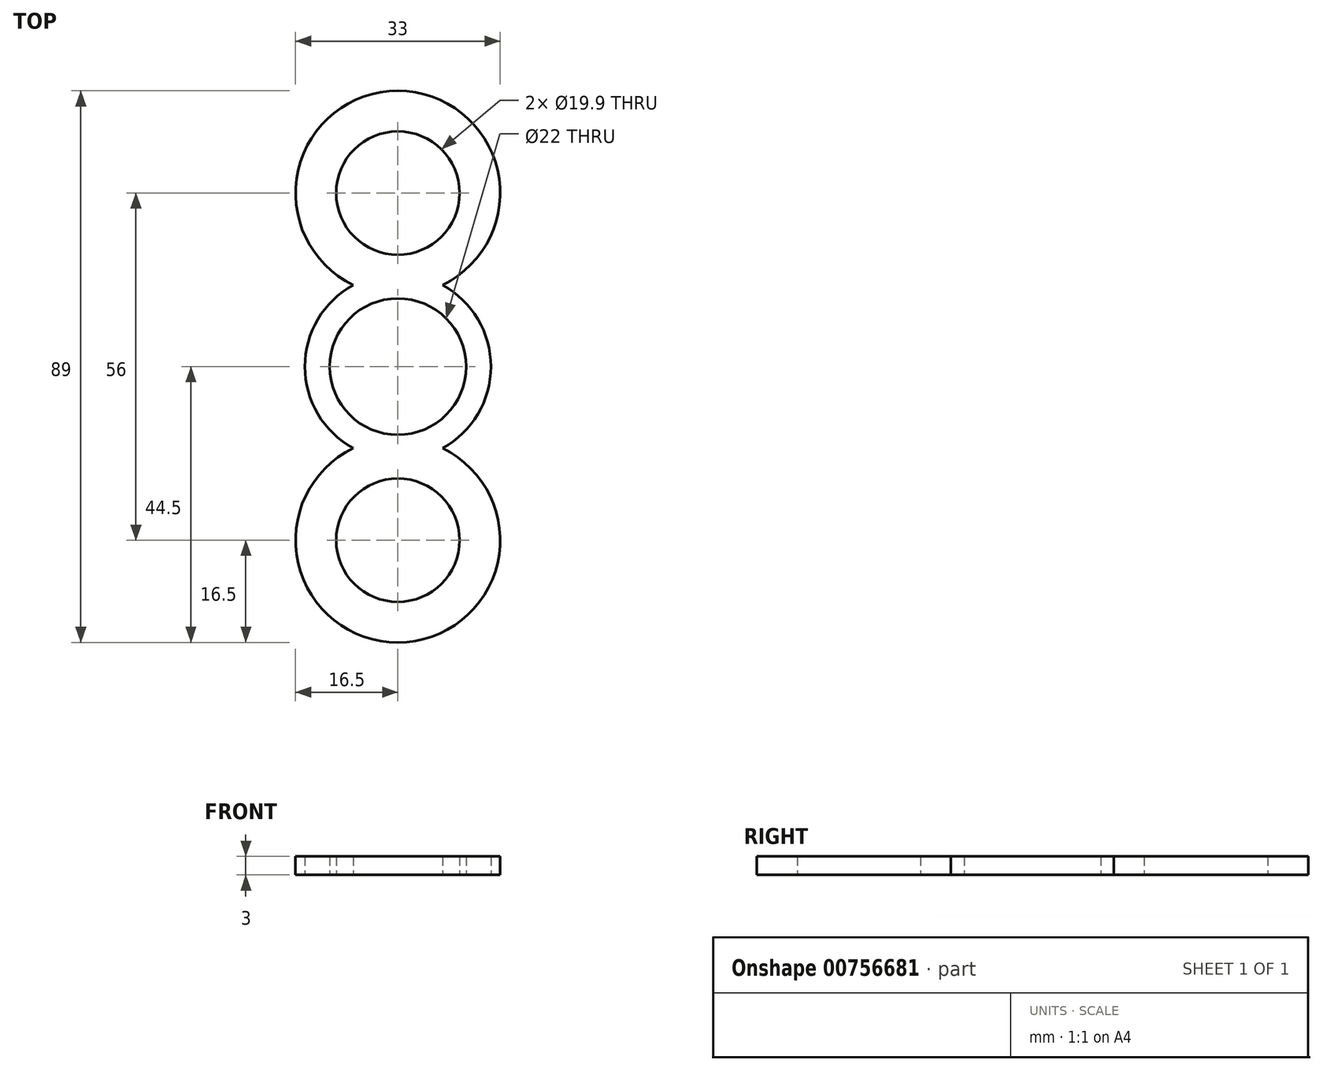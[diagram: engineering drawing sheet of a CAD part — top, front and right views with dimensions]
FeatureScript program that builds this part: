
annotation { "Feature Type Name" : "Feature", "Feature Type Description" : "" }
export const myFeature = defineFeature(function(context is Context, id is Id, definition is map)
    precondition{}
    {
        {
            var Q0;
            Q0=qCreatedBy(makeId("Top.planeOp"),FACE);
            var sketch = newSketch(context, id + "F0", { "sketchPlane" : qUnion([Q0])});
            skCircle(sketch, "E0", {"center": v(0, 0) * mm, "radius": 11 * mm});
            skArc(sketch, "E1", {"start": v(-7.2, 13.16) * mm, "mid": v(-15, 0) * mm, "end": v(-7.2, -13.16) * mm});
            skLineSegment(sketch, "E2", {"start": v(0, 11) * mm, "end": v(0, 11.5) * mm});
            skCircle(sketch, "E3", {"center": v(0, 28) * mm, "radius": 9.95 * mm});
            skArc(sketch, "E4", {"start": v(7.2, 13.16) * mm, "mid": v(0, 44.5) * mm, "end": v(-7.2, 13.16) * mm});
            skLineSegment(sketch, "E5", {"start": v(0, -11) * mm, "end": v(0, -11.5) * mm});
            skCircle(sketch, "E6", {"center": v(0, -28) * mm, "radius": 9.95 * mm});
            skArc(sketch, "E7.trimOffspring", {"start": v(7.2, -13.16) * mm, "mid": v(15, 0) * mm, "end": v(7.2, 13.16) * mm});
            skArc(sketch, "E8", {"start": v(-7.2, -13.16) * mm, "mid": v(0, -44.5) * mm, "end": v(7.2, -13.16) * mm});
            skSolve(sketch);
        }
        {
            var Q0;
            Q0=makeQuery(id+"F0.imprint","IMPRINT",FACE,{"disambiguationData":[TD([[makeQuery(id+"F0.imprint","IMPRINT",EDGE,{"derivedFrom":sQuery(id+"F0.wireOp",EDGE,"E1")}),1.0]])]});
            var Q1;
            Q1=sQuery(id+"F0.wireOp",EDGE,"E0");
            var Q2;
            Q2=sQuery(id+"F0.wireOp",EDGE,"E1");
            var Q3;
            Q3=sQuery(id+"F0.wireOp",EDGE,"E3");
            var Q4;
            Q4=sQuery(id+"F0.wireOp",EDGE,"E4");
            var Q5;
            Q5=sQuery(id+"F0.wireOp",EDGE,"E6");
            var Q6;
            Q6=sQuery(id+"F0.wireOp",EDGE,"E7.trimOffspring");
            var Q7;
            Q7=sQuery(id+"F0.wireOp",EDGE,"E8");
            var Q8;
            Q8=sQuery(id+"F0.wireOp",EDGE,"E5");
            var Q9;
            Q9=sQuery(id+"F0.wireOp",EDGE,"E2");
            extrude(context, id + "F1", {"entities" : qUnion([Q0]), "surfaceEntities" : qUnion([Q1, Q2, Q3, Q4, Q5, Q6, Q7, Q8, Q9]), "depth" : 3 * mm, "offsetDistance" : 25 * mm});
        }
    });
